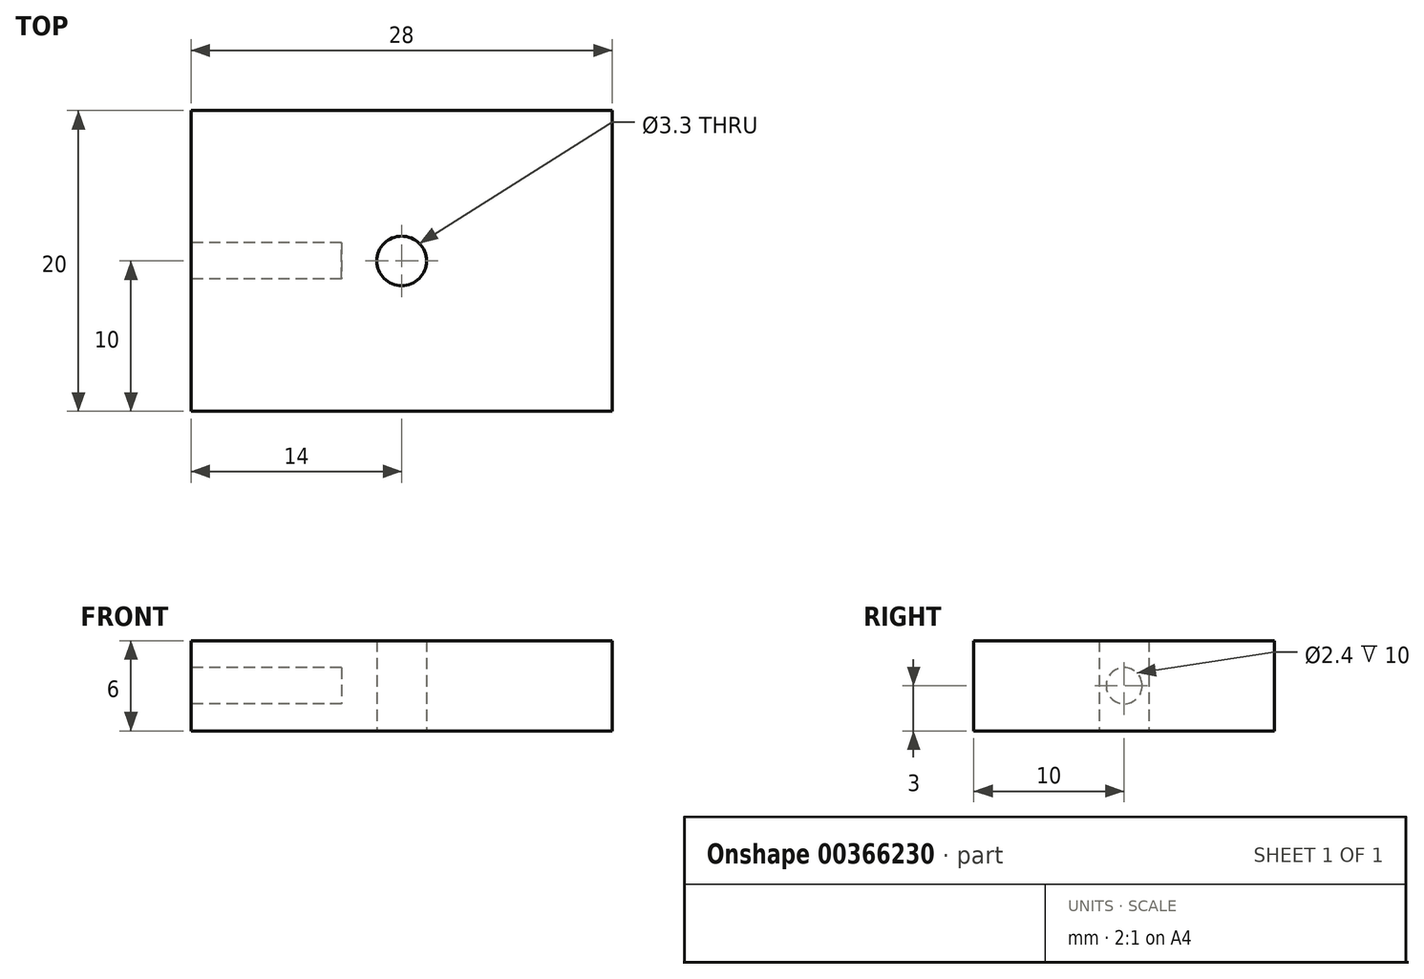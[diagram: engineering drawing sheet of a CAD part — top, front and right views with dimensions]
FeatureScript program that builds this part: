
annotation { "Feature Type Name" : "Feature", "Feature Type Description" : "" }
export const myFeature = defineFeature(function(context is Context, id is Id, definition is map)
    precondition{}
    {
        {
            var Q0;
            Q0=qCreatedBy(makeId("Top.planeOp"),FACE);
            var sketch = newSketch(context, id + "F0", { "sketchPlane" : qUnion([Q0])});
            skLineSegment(sketch, "E0.bottom", {"start": v(14, -10) * mm, "end": v(-14, -10) * mm});
            skLineSegment(sketch, "E0.top", {"start": v(14, 10) * mm, "end": v(-14, 10) * mm});
            skLineSegment(sketch, "E0.left", {"start": v(14, -10) * mm, "end": v(14, 10) * mm});
            skLineSegment(sketch, "E0.right", {"start": v(-14, -10) * mm, "end": v(-14, 10) * mm});
            skPoint(sketch, "E0.middle", {"position": v(0, 0) * mm});
            skCircle(sketch, "E1", {"center": v(0, 0) * mm, "radius": 1.65 * mm});
            skSolve(sketch);
        }
        {
            var Q0;
            Q0=makeQuery(id+"F0.imprint","IMPRINT",FACE,{"disambiguationData":[TD([[makeQuery(id+"F0.imprint","IMPRINT",EDGE,{"derivedFrom":sQuery(id+"F0.wireOp",EDGE,"E0.bottom")}),-1.0]])]});
            extrude(context, id + "F1", {"entities" : qUnion([Q0]), "depth" : 6 * mm});
        }
        {
            var Q0;
            Q0=makeQuery(id+"F1.opExtrude","SWEPT_FACE",FACE,{"disambiguationData":[OSD([sQuery(id+"F0.wireOp",EDGE,"E0.right")])]});
            var sketch = newSketch(context, id + "F2", { "sketchPlane" : qUnion([Q0])});
            skPoint(sketch, "E2", {"position": v(0, 3) * mm});
            skCircle(sketch, "E3", {"center": v(0, 3) * mm, "radius": 1.2 * mm});
            skSolve(sketch);
        }
        {
            var Q0;
            Q0=makeQuery(id+"F2.imprint","IMPRINT",FACE,{"disambiguationData":[TD([[makeQuery(id+"F2.imprint","IMPRINT",EDGE,{"derivedFrom":sQuery(id+"F2.wireOp",EDGE,"E3")}),1.0]])]});
            extrude(context, id + "F3", {"entities" : qUnion([Q0]), "operationType" : NewBodyOperationType.REMOVE, "oppositeDirection" : true, "depth" : 10 * mm});
        }
    });
